# Revit family: Architect_Series-Clad_Wood-Double-Hung_Vent_Unit Brick JK
name_source: partatom
category: Windows
revit_build: Autodesk Revit 2016 (Build: 20150714_1515(x64)
units: mm (PartAtom-declared; Revit-internal decimal feet)

## family parameters
Always vertical = Yes
Cut with Voids When Loaded = No
Host = Wall
Room Calculation Point = No
Shared = No

## types (80) — shared parameters
Analytic Construction = <None>
Architectural Data Sheet = To be determined
Architectural Design Manual = www.pellaadm.com
Brick Sill = <By Category>
Default Sill Height = 2' - 7 1/2"
Description = Double Hung - Vent Units
Exterior Finish = Pella-Exterior Clad-White
Glazing = 0' - 0 5/8"
Glazing Type = Pella-Clear Insulating Glass
Grille Finish = Pella-Exterior Clad-White
Interior Finish = Pella-Interior-No Primer
Manufacturer = Pella Windows & Doors
Series = Architect Series - Aluminum-Clad Wood
Set Back = 0' - 5 3/8"
Size Constraint = Window Sizing constraints available in 6.35 mm increments
URL = www.pella.com
Wall Closure = By host

## per-type parameters (varying)
| type | Checkrail Height | Head Height | Height | Rough Height | Rough Width | Sash Width | Unit Height | Unit Width | Width |
| 2135 | 1' - 5 7/8" | 5' - 6 1/2" | 2' - 11" | 2' - 11 3/4" | 1' - 9 3/4" | 1' - 6 1/8" | 2' - 11" | 1' - 9" | 1' - 9" |
| 2141 | 1' - 8 7/8" | 6' - 0 1/2" | 3' - 5" | 3' - 5 3/4" | 1' - 9 3/4" | 1' - 6 1/8" | 3' - 5" | 1' - 9" | 1' - 9" |
| 2147 | 1' - 11 7/8" | 6' - 6 1/2" | 3' - 11" | 3' - 11 3/4" | 1' - 9 3/4" | 1' - 6 1/8" | 3' - 11" | 1' - 9" | 1' - 9" |
| 2153 | 2' - 2 7/8" | 7' - 0 1/2" | 4' - 5" | 4' - 5 3/4" | 1' - 9 3/4" | 1' - 6 1/8" | 4' - 5" | 1' - 9" | 1' - 9" |
| 2157 | 2' - 4 7/8" | 7' - 4 1/2" | 4' - 9" | 4' - 9 3/4" | 1' - 9 3/4" | 1' - 6 1/8" | 4' - 9" | 1' - 9" | 1' - 9" |
| 2159 | 2' - 5 7/8" | 7' - 6 1/2" | 4' - 11" | 4' - 11 3/4" | 1' - 9 3/4" | 1' - 6 1/8" | 4' - 11" | 1' - 9" | 1' - 9" |
| 2165 | 2' - 8 7/8" | 8' - 0 1/2" | 5' - 5" | 5' - 5 3/4" | 1' - 9 3/4" | 1' - 6 1/8" | 5' - 5" | 1' - 9" | 1' - 9" |
| 2171 | 2' - 11 7/8" | 8' - 6 1/2" | 5' - 11" | 5' - 11 3/4" | 1' - 9 3/4" | 1' - 6 1/8" | 5' - 11" | 1' - 9" | 1' - 9" |
| 2177 | 3' - 2 7/8" | 9' - 0 1/2" | 6' - 5" | 6' - 5 3/4" | 1' - 9 3/4" | 1' - 6 1/8" | 6' - 5" | 1' - 9" | 1' - 9" |
| 2184 | 3' - 6 3/8" | 9' - 7 1/2" | 7' - 0" | 7' - 0 3/4" | 1' - 9 3/4" | 1' - 6 1/8" | 7' - 0" | 1' - 9" | 1' - 9" |
| 2535 | 1' - 5 7/8" | 5' - 6 1/2" | 2' - 11" | 2' - 11 3/4" | 2' - 1 3/4" | 1' - 10 1/8" | 2' - 11" | 2' - 1" | 2' - 1" |
| 2541 | 1' - 8 7/8" | 6' - 0 1/2" | 3' - 5" | 3' - 5 3/4" | 2' - 1 3/4" | 1' - 10 1/8" | 3' - 5" | 2' - 1" | 2' - 1" |
| 2547 | 1' - 11 7/8" | 6' - 6 1/2" | 3' - 11" | 3' - 11 3/4" | 2' - 1 3/4" | 1' - 10 1/8" | 3' - 11" | 2' - 1" | 2' - 1" |
| 2553 | 2' - 2 7/8" | 7' - 0 1/2" | 4' - 5" | 4' - 5 3/4" | 2' - 1 3/4" | 1' - 10 1/8" | 4' - 5" | 2' - 1" | 2' - 1" |
| 2557 | 2' - 4 7/8" | 7' - 4 1/2" | 4' - 9" | 4' - 9 3/4" | 2' - 1 3/4" | 1' - 10 1/8" | 4' - 9" | 2' - 1" | 2' - 1" |
| 2559 | 2' - 5 7/8" | 7' - 6 1/2" | 4' - 11" | 4' - 11 3/4" | 2' - 1 3/4" | 1' - 10 1/8" | 4' - 11" | 2' - 1" | 2' - 1" |
| 2565 | 2' - 8 7/8" | 8' - 0 1/2" | 5' - 5" | 5' - 5 3/4" | 2' - 1 3/4" | 1' - 10 1/8" | 5' - 5" | 2' - 1" | 2' - 1" |
| 2571 | 2' - 11 7/8" | 8' - 6 1/2" | 5' - 11" | 5' - 11 3/4" | 2' - 1 3/4" | 1' - 10 1/8" | 5' - 11" | 2' - 1" | 2' - 1" |
| 2577 | 3' - 2 7/8" | 9' - 0 1/2" | 6' - 5" | 6' - 5 3/4" | 2' - 1 3/4" | 1' - 10 1/8" | 6' - 5" | 2' - 1" | 2' - 1" |
| 2584 | 3' - 6 3/8" | 9' - 7 1/2" | 7' - 0" | 7' - 0 3/4" | 2' - 1 3/4" | 1' - 10 1/8" | 7' - 0" | 2' - 1" | 2' - 1" |
| 2935 | 1' - 5 7/8" | 5' - 6 1/2" | 2' - 11" | 2' - 11 3/4" | 2' - 5 3/4" | 2' - 2 1/8" | 2' - 11" | 2' - 5" | 2' - 5" |
| 2941 | 1' - 8 7/8" | 6' - 0 1/2" | 3' - 5" | 3' - 5 3/4" | 2' - 5 3/4" | 2' - 2 1/8" | 3' - 5" | 2' - 5" | 2' - 5" |
| 2947 | 1' - 11 7/8" | 6' - 6 1/2" | 3' - 11" | 3' - 11 3/4" | 2' - 5 3/4" | 2' - 2 1/8" | 3' - 11" | 2' - 5" | 2' - 5" |
| 2953 | 2' - 2 7/8" | 7' - 0 1/2" | 4' - 5" | 4' - 5 3/4" | 2' - 5 3/4" | 2' - 2 1/8" | 4' - 5" | 2' - 5" | 2' - 5" |
| 2957 | 2' - 4 7/8" | 7' - 4 1/2" | 4' - 9" | 4' - 9 3/4" | 2' - 5 3/4" | 2' - 2 1/8" | 4' - 9" | 2' - 5" | 2' - 5" |
| 2959 | 2' - 5 7/8" | 7' - 6 1/2" | 4' - 11" | 4' - 11 3/4" | 2' - 5 3/4" | 2' - 2 1/8" | 4' - 11" | 2' - 5" | 2' - 5" |
| 2965 | 2' - 8 7/8" | 8' - 0 1/2" | 5' - 5" | 5' - 5 3/4" | 2' - 5 3/4" | 2' - 2 1/8" | 5' - 5" | 2' - 5" | 2' - 5" |
| 2971 | 2' - 11 7/8" | 8' - 6 1/2" | 5' - 11" | 5' - 11 3/4" | 2' - 5 3/4" | 2' - 2 1/8" | 5' - 11" | 2' - 5" | 2' - 5" |
| 2977 | 3' - 2 7/8" | 9' - 0 1/2" | 6' - 5" | 6' - 5 3/4" | 2' - 5 3/4" | 2' - 2 1/8" | 6' - 5" | 2' - 5" | 2' - 5" |
| 2984 | 3' - 6 3/8" | 9' - 7 1/2" | 7' - 0" | 7' - 0 3/4" | 2' - 5 3/4" | 2' - 2 1/8" | 7' - 0" | 2' - 5" | 2' - 5" |
| 3335 | 1' - 5 7/8" | 5' - 6 1/2" | 2' - 11" | 2' - 11 3/4" | 2' - 9 3/4" | 2' - 6 1/8" | 2' - 11" | 2' - 9" | 2' - 9" |
| 3341 | 1' - 8 7/8" | 6' - 0 1/2" | 3' - 5" | 3' - 5 3/4" | 2' - 9 3/4" | 2' - 6 1/8" | 3' - 5" | 2' - 9" | 2' - 9" |
| 3347 | 1' - 11 7/8" | 6' - 6 1/2" | 3' - 11" | 3' - 11 3/4" | 2' - 9 3/4" | 2' - 6 1/8" | 3' - 11" | 2' - 9" | 2' - 9" |
| 3353 | 2' - 2 7/8" | 7' - 0 1/2" | 4' - 5" | 4' - 5 3/4" | 2' - 9 3/4" | 2' - 6 1/8" | 4' - 5" | 2' - 9" | 2' - 9" |
| 3357 | 2' - 4 7/8" | 7' - 4 1/2" | 4' - 9" | 4' - 9 3/4" | 2' - 9 3/4" | 2' - 6 1/8" | 4' - 9" | 2' - 9" | 2' - 9" |
| 3359 | 2' - 5 7/8" | 7' - 6 1/2" | 4' - 11" | 4' - 11 3/4" | 2' - 9 3/4" | 2' - 6 1/8" | 4' - 11" | 2' - 9" | 2' - 9" |
| 3365 | 2' - 8 7/8" | 8' - 0 1/2" | 5' - 5" | 5' - 5 3/4" | 2' - 9 3/4" | 2' - 6 1/8" | 5' - 5" | 2' - 9" | 2' - 9" |
| 3371 | 2' - 11 7/8" | 8' - 6 1/2" | 5' - 11" | 5' - 11 3/4" | 2' - 9 3/4" | 2' - 6 1/8" | 5' - 11" | 2' - 9" | 2' - 9" |
| 3377 | 3' - 2 7/8" | 9' - 0 1/2" | 6' - 5" | 6' - 5 3/4" | 2' - 9 3/4" | 2' - 6 1/8" | 6' - 5" | 2' - 9" | 2' - 9" |
| 3384 | 3' - 6 3/8" | 9' - 7 1/2" | 7' - 0" | 7' - 0 3/4" | 2' - 11 3/4" | 2' - 8 1/8" | 7' - 0" | 2' - 11" | 2' - 11" |
| 3735 | 1' - 5 7/8" | 5' - 6 1/2" | 2' - 11" | 2' - 11 3/4" | 3' - 1 3/4" | 2' - 10 1/8" | 2' - 11" | 3' - 1" | 3' - 1" |
| 3741 | 1' - 8 7/8" | 6' - 0 1/2" | 3' - 5" | 3' - 5 3/4" | 3' - 1 3/4" | 2' - 10 1/8" | 3' - 5" | 3' - 1" | 3' - 1" |
| 3747 | 1' - 11 7/8" | 6' - 6 1/2" | 3' - 11" | 3' - 11 3/4" | 3' - 1 3/4" | 2' - 10 1/8" | 3' - 11" | 3' - 1" | 3' - 1" |
| 3753 | 2' - 2 7/8" | 7' - 0 1/2" | 4' - 5" | 4' - 5 3/4" | 3' - 1 3/4" | 2' - 10 1/8" | 4' - 5" | 3' - 1" | 3' - 1" |
| 3757 | 2' - 4 7/8" | 7' - 4 1/2" | 4' - 9" | 4' - 9 3/4" | 3' - 1 3/4" | 2' - 10 1/8" | 4' - 9" | 3' - 1" | 3' - 1" |
| 3759 | 2' - 5 7/8" | 7' - 6 1/2" | 4' - 11" | 4' - 11 3/4" | 3' - 1 3/4" | 2' - 10 1/8" | 4' - 11" | 3' - 1" | 3' - 1" |
| 3765 | 2' - 8 7/8" | 8' - 0 1/2" | 5' - 5" | 5' - 5 3/4" | 3' - 1 3/4" | 2' - 10 1/8" | 5' - 5" | 3' - 1" | 3' - 1" |
| 3771 | 2' - 11 7/8" | 8' - 6 1/2" | 5' - 11" | 5' - 11 3/4" | 3' - 1 3/4" | 2' - 10 1/8" | 5' - 11" | 3' - 1" | 3' - 1" |
| 3777 | 3' - 2 7/8" | 9' - 0 1/2" | 6' - 5" | 6' - 5 3/4" | 3' - 1 3/4" | 2' - 10 1/8" | 6' - 5" | 3' - 1" | 3' - 1" |
| 3784 | 3' - 6 3/8" | 9' - 7 1/2" | 7' - 0" | 7' - 0 3/4" | 3' - 1 3/4" | 2' - 10 1/8" | 7' - 0" | 3' - 1" | 3' - 1" |
| 4135 | 1' - 5 7/8" | 5' - 6 1/2" | 2' - 11" | 2' - 11 3/4" | 3' - 5 3/4" | 3' - 2 1/8" | 2' - 11" | 3' - 5" | 3' - 5" |
| 4141 | 1' - 8 7/8" | 6' - 0 1/2" | 3' - 5" | 3' - 5 3/4" | 3' - 5 3/4" | 3' - 2 1/8" | 3' - 5" | 3' - 5" | 3' - 5" |
| 4147 | 1' - 11 7/8" | 6' - 6 1/2" | 3' - 11" | 3' - 11 3/4" | 3' - 5 3/4" | 3' - 2 1/8" | 3' - 11" | 3' - 5" | 3' - 5" |
| 4153 | 2' - 2 7/8" | 7' - 0 1/2" | 4' - 5" | 4' - 5 3/4" | 3' - 5 3/4" | 3' - 2 1/8" | 4' - 5" | 3' - 5" | 3' - 5" |
| 4157 | 2' - 4 7/8" | 7' - 4 1/2" | 4' - 9" | 4' - 9 3/4" | 3' - 5 3/4" | 3' - 2 1/8" | 4' - 9" | 3' - 5" | 3' - 5" |
| 4159 | 2' - 5 7/8" | 7' - 6 1/2" | 4' - 11" | 4' - 11 3/4" | 3' - 5 3/4" | 3' - 2 1/8" | 4' - 11" | 3' - 5" | 3' - 5" |
| 4165 | 2' - 8 7/8" | 8' - 0 1/2" | 5' - 5" | 5' - 5 3/4" | 3' - 5 3/4" | 3' - 2 1/8" | 5' - 5" | 3' - 5" | 3' - 5" |
| 4171 | 2' - 11 7/8" | 8' - 6 1/2" | 5' - 11" | 5' - 11 3/4" | 3' - 5 3/4" | 3' - 2 1/8" | 5' - 11" | 3' - 5" | 3' - 5" |
| 4177 | 3' - 2 7/8" | 9' - 0 1/2" | 6' - 5" | 6' - 5 3/4" | 3' - 5 3/4" | 3' - 2 1/8" | 6' - 5" | 3' - 5" | 3' - 5" |
| 4184 | 3' - 6 3/8" | 9' - 7 1/2" | 7' - 0" | 7' - 0 3/4" | 3' - 5 3/4" | 3' - 2 1/8" | 7' - 0" | 3' - 5" | 3' - 5" |
| 4535 | 1' - 5 7/8" | 5' - 6 1/2" | 2' - 11" | 2' - 11 3/4" | 3' - 9 3/4" | 3' - 6 1/8" | 2' - 11" | 3' - 9" | 3' - 9" |
| 4541 | 1' - 8 7/8" | 6' - 0 1/2" | 3' - 5" | 3' - 5 3/4" | 3' - 9 3/4" | 3' - 6 1/8" | 3' - 5" | 3' - 9" | 3' - 9" |
| 4547 | 1' - 11 7/8" | 6' - 6 1/2" | 3' - 11" | 3' - 11 3/4" | 3' - 9 3/4" | 3' - 6 1/8" | 3' - 11" | 3' - 9" | 3' - 9" |
| 4553 | 2' - 2 7/8" | 7' - 0 1/2" | 4' - 5" | 4' - 5 3/4" | 3' - 9 3/4" | 3' - 6 1/8" | 4' - 5" | 3' - 9" | 3' - 9" |
| 4557 | 2' - 4 7/8" | 7' - 4 1/2" | 4' - 9" | 4' - 9 3/4" | 3' - 9 3/4" | 3' - 6 1/8" | 4' - 9" | 3' - 9" | 3' - 9" |
| 4559 | 2' - 5 7/8" | 7' - 6 1/2" | 4' - 11" | 4' - 11 3/4" | 3' - 9 3/4" | 3' - 6 1/8" | 4' - 11" | 3' - 9" | 3' - 9" |
| 4565 | 2' - 8 7/8" | 8' - 0 1/2" | 5' - 5" | 5' - 5 3/4" | 3' - 9 3/4" | 3' - 6 1/8" | 5' - 5" | 3' - 9" | 3' - 9" |
| 4571 | 2' - 11 7/8" | 8' - 6 1/2" | 5' - 11" | 5' - 11 3/4" | 3' - 9 3/4" | 3' - 6 1/8" | 5' - 11" | 3' - 9" | 3' - 9" |
| 4577 | 3' - 2 7/8" | 9' - 0 1/2" | 6' - 5" | 6' - 5 3/4" | 3' - 9 3/4" | 3' - 6 1/8" | 6' - 5" | 3' - 9" | 3' - 9" |
| 4584 | 3' - 6 3/8" | 9' - 7 1/2" | 7' - 0" | 7' - 0 3/4" | 3' - 9 3/4" | 3' - 6 1/8" | 7' - 0" | 3' - 9" | 3' - 9" |
| 4835 | 1' - 5 7/8" | 5' - 6 1/2" | 2' - 11" | 2' - 11 3/4" | 4' - 0 3/4" | 3' - 9 1/8" | 2' - 11" | 4' - 0" | 4' - 0" |
| 4841 | 1' - 8 7/8" | 6' - 0 1/2" | 3' - 5" | 3' - 5 3/4" | 4' - 0 3/4" | 3' - 9 1/8" | 3' - 5" | 4' - 0" | 4' - 0" |
| 4847 | 1' - 11 7/8" | 6' - 6 1/2" | 3' - 11" | 3' - 11 3/4" | 4' - 0 3/4" | 3' - 9 1/8" | 3' - 11" | 4' - 0" | 4' - 0" |
| 4853 | 2' - 2 7/8" | 7' - 0 1/2" | 4' - 5" | 4' - 5 3/4" | 4' - 0 3/4" | 3' - 9 1/8" | 4' - 5" | 4' - 0" | 4' - 0" |
| 4857 | 2' - 4 7/8" | 7' - 4 1/2" | 4' - 9" | 4' - 9 3/4" | 4' - 0 3/4" | 3' - 9 1/8" | 4' - 9" | 4' - 0" | 4' - 0" |
| 4859 | 2' - 5 7/8" | 7' - 6 1/2" | 4' - 11" | 4' - 11 3/4" | 4' - 0 3/4" | 3' - 9 1/8" | 4' - 11" | 4' - 0" | 4' - 0" |
| 4865 | 2' - 8 7/8" | 8' - 0 1/2" | 5' - 5" | 5' - 5 3/4" | 4' - 0 3/4" | 3' - 9 1/8" | 5' - 5" | 4' - 0" | 4' - 0" |
| 4871 | 2' - 11 7/8" | 8' - 6 1/2" | 5' - 11" | 5' - 11 3/4" | 4' - 0 3/4" | 3' - 9 1/8" | 5' - 11" | 4' - 0" | 4' - 0" |
| 4877 | 3' - 2 7/8" | 9' - 0 1/2" | 6' - 5" | 6' - 5 3/4" | 4' - 0 3/4" | 3' - 9 1/8" | 6' - 5" | 4' - 0" | 4' - 0" |
| 4884 | 3' - 6 3/8" | 9' - 7 1/2" | 7' - 0" | 7' - 0 3/4" | 4' - 0 3/4" | 3' - 9 1/8" | 7' - 0" | 4' - 0" | 4' - 0" |

note: column(s) folded — value = type name in every type: Model

## geometry (parser evidence)
native form markers: Blend x2, Sweep x3
no freeform markers — native parametric forms only
